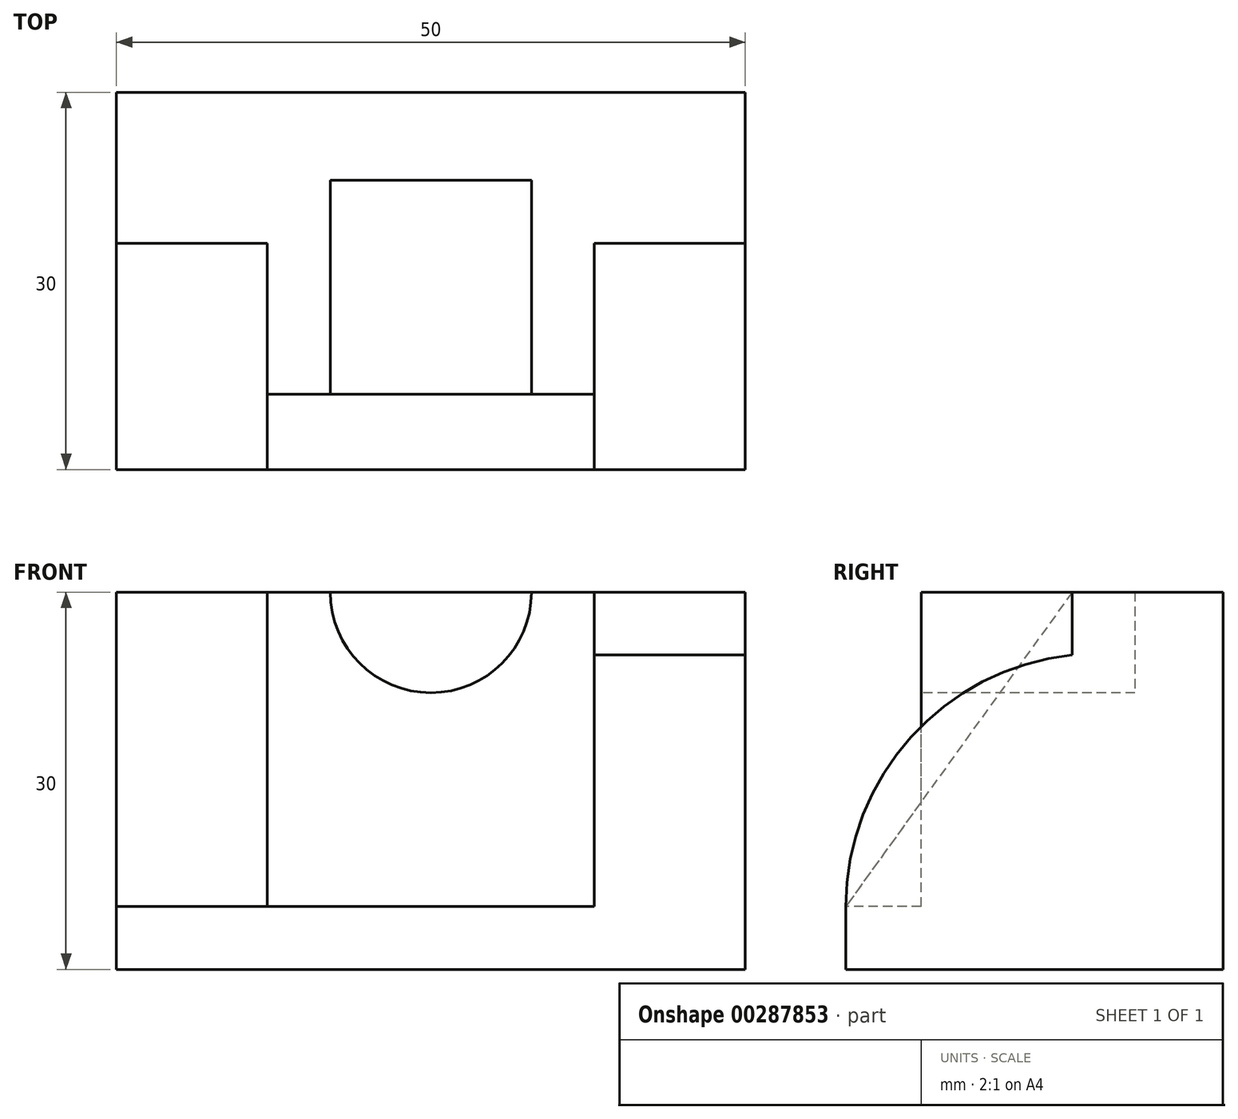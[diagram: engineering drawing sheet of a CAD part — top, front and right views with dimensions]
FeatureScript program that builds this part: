
annotation { "Feature Type Name" : "Feature", "Feature Type Description" : "" }
export const myFeature = defineFeature(function(context is Context, id is Id, definition is map)
    precondition{}
    {
        {
            var Q0;
            Q0=qCreatedBy(makeId("Right.planeOp"),FACE);
            var sketch = newSketch(context, id + "F0", { "sketchPlane" : qUnion([Q0])});
            skLineSegment(sketch, "E0.bottom", {"start": v(0, 0) * mm, "end": v(30, 0) * mm});
            skLineSegment(sketch, "E0.top", {"start": v(0, 30) * mm, "end": v(30, 30) * mm});
            skLineSegment(sketch, "E0.left", {"start": v(0, 0) * mm, "end": v(0, 30) * mm});
            skLineSegment(sketch, "E0.right", {"start": v(30, 0) * mm, "end": v(30, 30) * mm});
            skSolve(sketch);
        }
        {
            var Q0;
            Q0 = qSketchRegion(id + "F0", true);
            extrude(context, id + "F1", {"entities" : qUnion([Q0]), "depth" : 50 * mm});
        }
        {
            var Q0;
            Q0=makeQuery(id+"F1.opExtrude","CAP_FACE",FACE,{"disambiguationData":[OSD([sQuery(id+"F0.wireOp",EDGE,"E0.bottom"),sQuery(id+"F0.wireOp",EDGE,"E0.top"),sQuery(id+"F0.wireOp",EDGE,"E0.left"),sQuery(id+"F0.wireOp",EDGE,"E0.right")])],"isStart":false});
            var sketch = newSketch(context, id + "F2", { "sketchPlane" : qUnion([Q0])});
            skLineSegment(sketch, "E1.0", {"start": v(30, 0) * mm, "end": v(30, 30) * mm});
            skLineSegment(sketch, "E2.0", {"start": v(0, 0) * mm, "end": v(30, 0) * mm});
            skLineSegment(sketch, "E3", {"start": v(30, 30) * mm, "end": v(18, 30) * mm});
            skLineSegment(sketch, "E4", {"start": v(18, 30) * mm, "end": v(18, 25) * mm});
            skLineSegment(sketch, "E5", {"start": v(0, 0) * mm, "end": v(0, 5) * mm});
            skArc(sketch, "E6", {"start": v(18, 25) * mm, "mid": v(5.16, 18.45) * mm, "end": v(0, 5) * mm});
            skSolve(sketch);
        }
        {
            var Q0;
            {var subQ0=sQuery(id+"F2.wireOp",EDGE,"E4");Q0=makeQuery(id+"F2.imprint","IMPRINT",FACE,{"disambiguationData":[TD([[makeQuery(id+"F2.imprint","IMPRINT",EDGE,{"derivedFrom":subQ0}),-1.0]])]});}
            extrude(context, id + "F3", {"entities" : qUnion([Q0]), "operationType" : NewBodyOperationType.REMOVE, "oppositeDirection" : true, "depth" : 12 * mm});
        }
        {
            var Q0;
            Q0=makeQuery(id+"F1.opExtrude","CAP_FACE",FACE,{"disambiguationData":[OSD([sQuery(id+"F0.wireOp",EDGE,"E0.bottom"),sQuery(id+"F0.wireOp",EDGE,"E0.top"),sQuery(id+"F0.wireOp",EDGE,"E0.left"),sQuery(id+"F0.wireOp",EDGE,"E0.right")])],"isStart":true});
            var sketch = newSketch(context, id + "F4", { "sketchPlane" : qUnion([Q0])});
            skLineSegment(sketch, "E7.0", {"start": v(-18, 30) * mm, "end": v(-30, 30) * mm});
            skLineSegment(sketch, "E8.0", {"start": v(0, 0) * mm, "end": v(0, 5) * mm});
            skLineSegment(sketch, "E9", {"start": v(-18, 30) * mm, "end": v(0, 5) * mm});
            skSolve(sketch);
        }
        {
            var Q0;
            {var subQ0=sQuery(id+"F4.wireOp",EDGE,"E9");Q0=makeQuery(id+"F4.imprint","IMPRINT",FACE,{"disambiguationData":[TD([[makeQuery(id+"F4.imprint","IMPRINT",EDGE,{"derivedFrom":subQ0}),1.0]])]});}
            extrude(context, id + "F5", {"entities" : qUnion([Q0]), "operationType" : NewBodyOperationType.REMOVE, "flatOperationType" : FlatOperationType.REMOVE, "oppositeDirection" : true, "offsetDistance" : 25 * mm, "depth" : 12 * mm, "domain" : OperationDomain.MODEL});
        }
        {
            var Q0;
            Q0=makeQuery(id+"F1.opExtrude","SWEPT_FACE",FACE,{"disambiguationData":[OSD([sQuery(id+"F0.wireOp",EDGE,"E0.left")])]});
            var sketch = newSketch(context, id + "F6", { "sketchPlane" : qUnion([Q0])});
            skLineSegment(sketch, "E10", {"start": v(12, 5) * mm, "end": v(38, 5) * mm});
            skLineSegment(sketch, "E11", {"start": v(38, 5) * mm, "end": v(38, 30) * mm});
            skLineSegment(sketch, "E12", {"start": v(38, 30) * mm, "end": v(12, 30) * mm});
            skLineSegment(sketch, "E13", {"start": v(12, 30) * mm, "end": v(12, 5) * mm});
            skArc(sketch, "E14", {"start": v(17, 30) * mm, "mid": v(25, 22) * mm, "end": v(33, 30) * mm});
            skSolve(sketch);
        }
        {
            var Q0;
            Q0 = qSketchRegion(id + "F6", true);
            extrude(context, id + "F7", {"entities" : qUnion([Q0]), "operationType" : NewBodyOperationType.REMOVE, "oppositeDirection" : true, "depth" : 6 * mm});
        }
        {
            var Q0;
            {var subQ0=sQuery(id+"F6.wireOp",EDGE,"E14");Q0=makeQuery(id+"F6.imprint","IMPRINT",FACE,{"disambiguationData":[TD([[makeQuery(id+"F6.imprint","IMPRINT",EDGE,{"derivedFrom":subQ0}),1.0]])]});}
            extrude(context, id + "F8", {"entities" : qUnion([Q0]), "operationType" : NewBodyOperationType.REMOVE, "oppositeDirection" : true, "depth" : 23 * mm});
        }
    });
